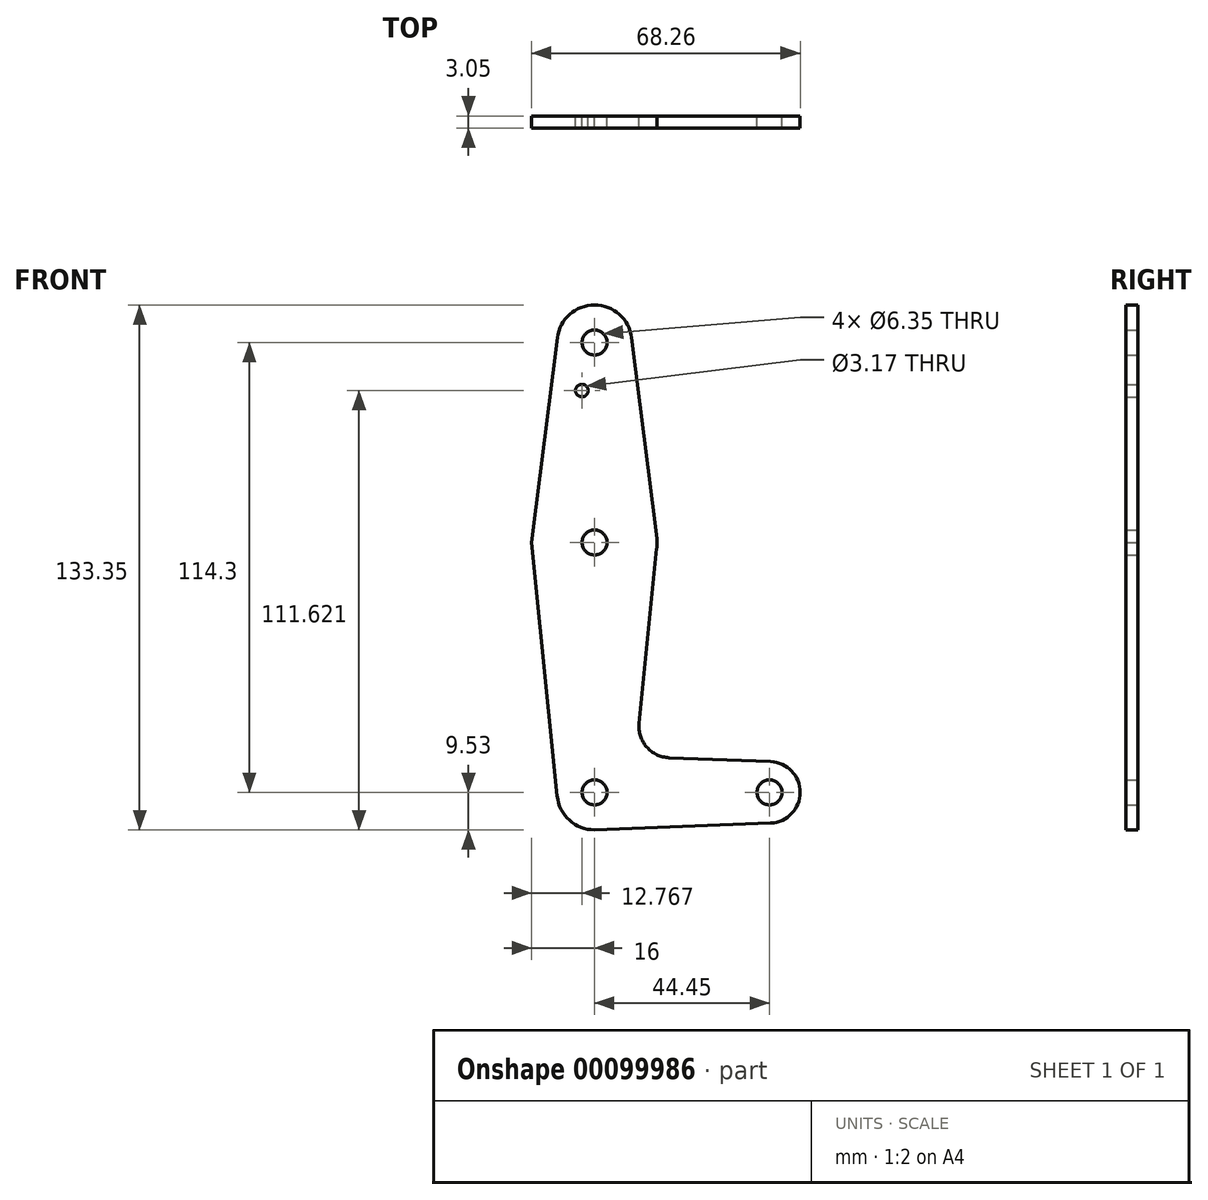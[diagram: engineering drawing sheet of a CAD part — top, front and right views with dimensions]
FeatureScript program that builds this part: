
annotation { "Feature Type Name" : "Feature", "Feature Type Description" : "" }
export const myFeature = defineFeature(function(context is Context, id is Id, definition is map)
    precondition{}
    {
        {
            var Q0;
            Q0=qCreatedBy(makeId("Front.planeOp"),FACE);
            var sketch = newSketch(context, id + "F0", { "sketchPlane" : qUnion([Q0])});
            skLineSegment(sketch, "E0", {"start": v(0, 50.8) * mm, "end": v(0, -63.5) * mm});
            skLineSegment(sketch, "E1", {"start": v(0, -63.5) * mm, "end": v(44.45, -63.5) * mm});
            skCircle(sketch, "E2", {"center": v(0, 50.8) * mm, "radius": 9.53 * mm});
            skCircle(sketch, "E3", {"center": v(0, 0) * mm, "radius": 15.88 * mm});
            skCircle(sketch, "E4", {"center": v(0, -63.5) * mm, "radius": 9.53 * mm});
            skCircle(sketch, "E5", {"center": v(44.45, -63.5) * mm, "radius": 7.8 * mm});
            skLineSegment(sketch, "E6", {"start": v(0, 0) * mm, "end": v(0, -63.5) * mm});
            skLineSegment(sketch, "E7", {"start": v(-9.45, 52) * mm, "end": v(-16, 0) * mm});
            skLineSegment(sketch, "E8", {"start": v(9.45, 52) * mm, "end": v(16, 0) * mm});
            skLineSegment(sketch, "E9", {"start": v(-16, 0) * mm, "end": v(-9.48, -64.46) * mm});
            skLineSegment(sketch, "E10", {"start": v(15.8, -1.59) * mm, "end": v(11.34, -45.97) * mm});
            skLineSegment(sketch, "E11", {"start": v(0, -73.03) * mm, "end": v(44.75, -71.3) * mm});
            skLineSegment(sketch, "E12", {"start": v(18.94, -54.7) * mm, "end": v(44.75, -55.7) * mm});
            skCircle(sketch, "E13", {"center": v(0, 50.8) * mm, "radius": 3.18 * mm});
            skCircle(sketch, "E14", {"center": v(-3.23, 38.6) * mm, "radius": 1.59 * mm});
            skCircle(sketch, "E15", {"center": v(0, 0) * mm, "radius": 3.18 * mm});
            skCircle(sketch, "E16", {"center": v(0, -63.5) * mm, "radius": 3.18 * mm});
            skCircle(sketch, "E17", {"center": v(44.45, -63.5) * mm, "radius": 3.18 * mm});
            skPoint(sketch, "E18.newPointB", {"position": v(0, -53.98) * mm});
            skArc(sketch, "E18.filletArc", {"start": v(11.34, -45.97) * mm, "mid": v(13.25, -51.98) * mm, "end": v(18.94, -54.7) * mm});
            skSolve(sketch);
        }
        {
            var Q0;
            {var subQ0=sQuery(id+"F0.wireOp",EDGE,"E11");var subQ1=sQuery(id+"F0.wireOp",EDGE,"E4");var subQ2=makeQuery(id+"F0.imprint","INTERSECT",VERTEX,{"disambiguationData":[OD(0.0)],"derivedFrom":[subQ1,subQ0]});Q0=makeQuery(id+"F0.imprint","IMPRINT",FACE,{"disambiguationData":[TD([[makeQuery(id+"F0.imprint","IMPRINT",EDGE,{"disambiguationData":[TD([[subQ2,-1.0]])],"derivedFrom":subQ1}),1.0]])]});}
            var Q1;
            {var subQ0=sQuery(id+"F0.wireOp",EDGE,"E2");var subQ1=sQuery(id+"F0.wireOp",EDGE,"E0");var subQ2=makeQuery(id+"F0.imprint","INTERSECT",VERTEX,{"derivedFrom":[subQ1,subQ0]});Q1=makeQuery(id+"F0.imprint","IMPRINT",FACE,{"disambiguationData":[TD([[makeQuery(id+"F0.imprint","IMPRINT",EDGE,{"disambiguationData":[TD([[subQ2,-1.0]])],"derivedFrom":subQ1}),1.0]])]});}
            var Q2;
            {var subQ0=sQuery(id+"F0.wireOp",EDGE,"E5");var subQ1=sQuery(id+"F0.wireOp",EDGE,"E1");var subQ2=makeQuery(id+"F0.imprint","INTERSECT",VERTEX,{"derivedFrom":[subQ1,subQ0]});Q2=makeQuery(id+"F0.imprint","IMPRINT",FACE,{"disambiguationData":[TD([[makeQuery(id+"F0.imprint","IMPRINT",EDGE,{"disambiguationData":[TD([[subQ2,1.0]])],"derivedFrom":subQ1}),-1.0]])]});}
            var Q3;
            Q3=makeQuery(id+"F0.imprint","IMPRINT",FACE,{"disambiguationData":[TD([[makeQuery(id+"F0.imprint","IMPRINT",EDGE,{"derivedFrom":sQuery(id+"F0.wireOp",EDGE,"E13")}),-1.0]])]});
            var Q4;
            {var subQ0=sQuery(id+"F0.wireOp",EDGE,"E9");Q4=makeQuery(id+"F0.imprint","IMPRINT",FACE,{"disambiguationData":[TD([[makeQuery(id+"F0.imprint","IMPRINT",EDGE,{"derivedFrom":subQ0}),1.0]])]});}
            var Q5;
            Q5=makeQuery(id+"F0.imprint","IMPRINT",FACE,{"disambiguationData":[TD([[makeQuery(id+"F0.imprint","IMPRINT",EDGE,{"derivedFrom":sQuery(id+"F0.wireOp",EDGE,"E17")}),-1.0]])]});
            var Q6;
            Q6=makeQuery(id+"F0.imprint","IMPRINT",FACE,{"disambiguationData":[TD([[makeQuery(id+"F0.imprint","IMPRINT",EDGE,{"derivedFrom":sQuery(id+"F0.wireOp",EDGE,"E14")}),-1.0]])]});
            var Q7;
            {var subQ0=sQuery(id+"F0.wireOp",EDGE,"E3");var subQ4=sQuery(id+"F0.wireOp",EDGE,"E0");var subQ9=makeQuery(id+"F0.imprint","INTERSECT",VERTEX,{"derivedFrom":[subQ4,subQ0]});Q7=makeQuery(id+"F0.imprint","IMPRINT",FACE,{"disambiguationData":[TD([[makeQuery(id+"F0.imprint","IMPRINT",EDGE,{"disambiguationData":[TD([[subQ9,-1.0]])],"derivedFrom":subQ4}),1.0]])]});}
            var Q8;
            {var subQ0=sQuery(id+"F0.wireOp",EDGE,"E3");var subQ4=sQuery(id+"F0.wireOp",EDGE,"E0");var subQ5=makeQuery(id+"F0.imprint","INTERSECT",VERTEX,{"derivedFrom":[subQ4,subQ0]});Q8=makeQuery(id+"F0.imprint","IMPRINT",FACE,{"disambiguationData":[TD([[makeQuery(id+"F0.imprint","IMPRINT",EDGE,{"disambiguationData":[TD([[subQ5,-1.0]])],"derivedFrom":subQ4}),-1.0]])]});}
            var Q9;
            {var subQ3=sQuery(id+"F0.wireOp",EDGE,"E1");var subQ7=sQuery(id+"F0.wireOp",EDGE,"E16");var subQ11=makeQuery(id+"F0.imprint","INTERSECT",VERTEX,{"derivedFrom":[subQ3,subQ7]});Q9=makeQuery(id+"F0.imprint","IMPRINT",FACE,{"disambiguationData":[TD([[makeQuery(id+"F0.imprint","IMPRINT",EDGE,{"disambiguationData":[TD([[subQ11,-1.0]])],"derivedFrom":subQ3}),-1.0]])]});}
            var Q10;
            {var subQ5=sQuery(id+"F0.wireOp",EDGE,"E10");Q10=makeQuery(id+"F0.imprint","IMPRINT",FACE,{"disambiguationData":[TD([[makeQuery(id+"F0.imprint","IMPRINT",EDGE,{"derivedFrom":subQ5}),-1.0]])]});}
            var Q11;
            {var subQ0=sQuery(id+"F0.wireOp",EDGE,"E16");var subQ1=sQuery(id+"F0.wireOp",EDGE,"E1");var subQ2=makeQuery(id+"F0.imprint","INTERSECT",VERTEX,{"derivedFrom":[subQ1,subQ0]});Q11=makeQuery(id+"F0.imprint","IMPRINT",FACE,{"disambiguationData":[TD([[makeQuery(id+"F0.imprint","IMPRINT",EDGE,{"disambiguationData":[TD([[subQ2,-1.0]])],"derivedFrom":subQ1}),1.0]])]});}
            extrude(context, id + "F1", {"entities" : qUnion([Q0, Q1, Q2, Q3, Q4, Q5, Q6, Q7, Q8, Q9, Q10, Q11]), "depth" : 3.05 * mm});
        }
    });
